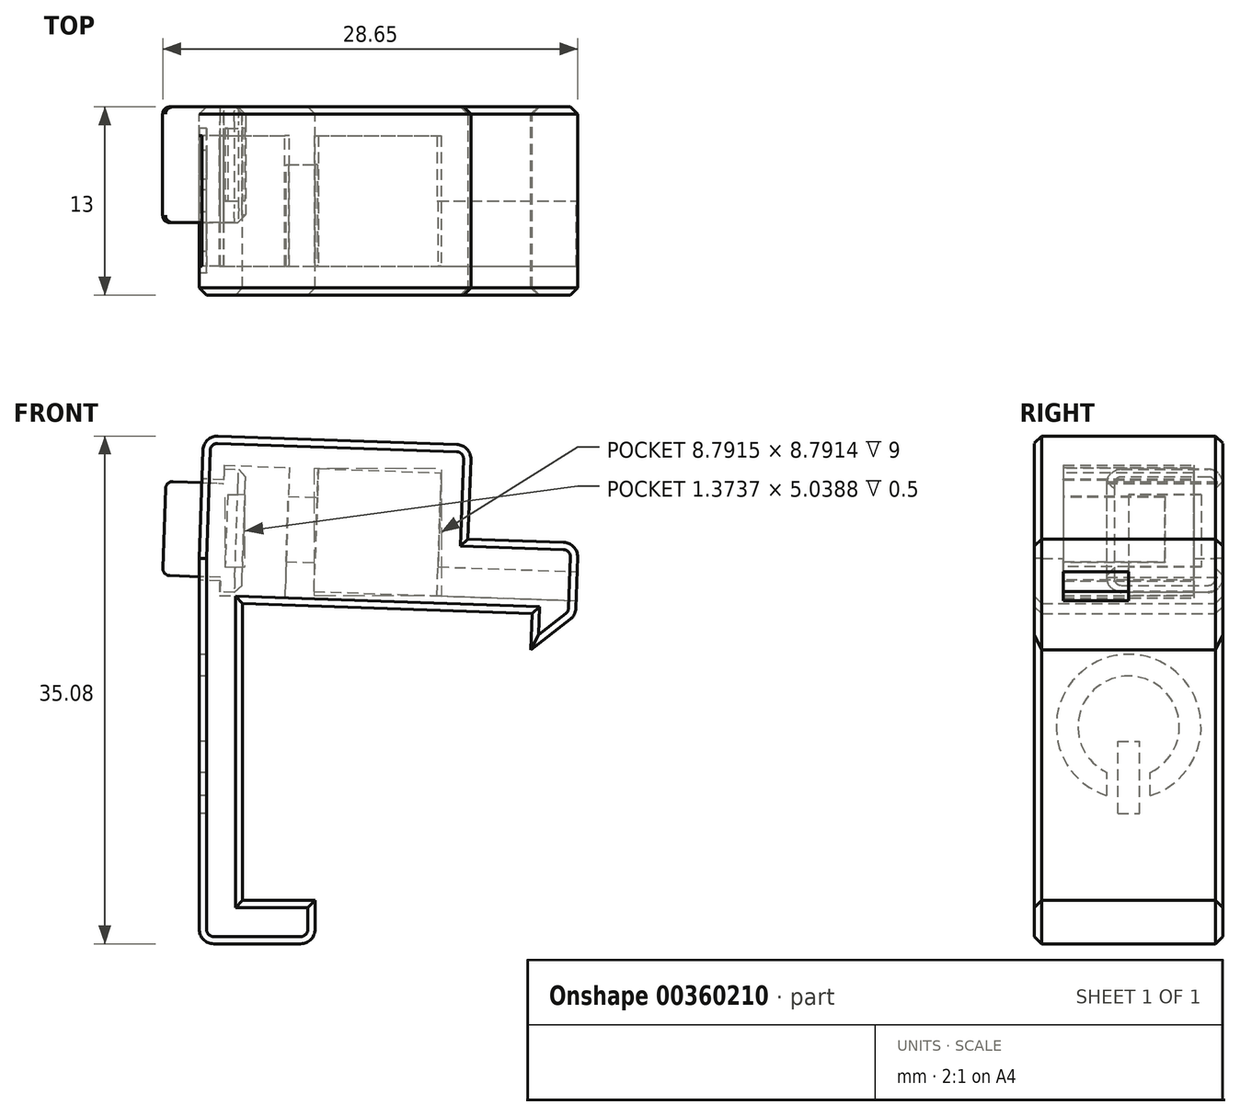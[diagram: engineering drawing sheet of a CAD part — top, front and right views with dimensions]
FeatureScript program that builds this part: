
annotation { "Feature Type Name" : "Feature", "Feature Type Description" : "" }
export const myFeature = defineFeature(function(context is Context, id is Id, definition is map)
    precondition{}
    {
        {
            var Q0;
            Q0=qCreatedBy(makeId("Front.planeOp"),FACE);
            var sketch = newSketch(context, id + "F0", { "sketchPlane" : qUnion([Q0])});
            skLineSegment(sketch, "E0", {"start": v(5, 0) * mm, "end": v(0, 0) * mm});
            skLineSegment(sketch, "E1", {"start": v(0, 0) * mm, "end": v(0, 20.51) * mm});
            skLineSegment(sketch, "E2", {"start": v(0, 20.51) * mm, "end": v(19.99, 19.81) * mm});
            skLineSegment(sketch, "E3", {"start": v(19.99, 19.81) * mm, "end": v(19.9, 17.32) * mm});
            skLineSegment(sketch, "E4", {"start": v(19.9, 17.32) * mm, "end": v(22.99, 19.7) * mm});
            skLineSegment(sketch, "E5", {"start": v(22.99, 19.7) * mm, "end": v(23.1, 22.7) * mm});
            skLineSegment(sketch, "E6", {"start": v(23.1, 22.7) * mm, "end": v(-3, 23.62) * mm});
            skLineSegment(sketch, "E7", {"start": v(-3, 23.62) * mm, "end": v(-3, -3) * mm});
            skLineSegment(sketch, "E8", {"start": v(-3, -3) * mm, "end": v(5, -3) * mm});
            skLineSegment(sketch, "E9", {"start": v(5, -3) * mm, "end": v(5, 0) * mm});
            skPoint(sketch, "E10.orphan", {"position": v(0, 20.51) * mm});
            skSolve(sketch);
        }
        {
            var Q0;
            Q0=qSketchRegion(id+"F0",true);
            extrude(context, id + "F1", {"entities" : qUnion([Q0]), "depth" : 13 * mm});
        }
        {
            var Q0;
            Q0=makeQuery(id+"F1.opExtrude","SWEPT_EDGE",EDGE,{"disambiguationData":[OSD([sQuery(id+"F0.wireOp",EDGE,"E8"),sQuery(id+"F0.wireOp",EDGE,"E9")])]});
            var Q1;
            Q1=makeQuery(id+"F1.opExtrude","SWEPT_EDGE",EDGE,{"disambiguationData":[OSD([sQuery(id+"F0.wireOp",EDGE,"E8"),sQuery(id+"F0.wireOp",EDGE,"E9")])]});
            var Q2;
            Q2=makeQuery(id+"F1.opExtrude","SWEPT_EDGE",EDGE,{"disambiguationData":[OSD([sQuery(id+"F0.wireOp",EDGE,"E4"),sQuery(id+"F0.wireOp",EDGE,"E5")])]});
            fillet(context, id + "F2", {"entities" : qUnion([Q0, Q1, Q2]), "radius" : 1 * mm, "tangentPropagation" : true, "allowEdgeOverflow" : false});
        }
        {
            var Q0;
            Q0=makeQuery(id+"F1.opExtrude","SWEPT_FACE",FACE,{"disambiguationData":[OSD([sQuery(id+"F0.wireOp",EDGE,"E6")])]});
            var sketch = newSketch(context, id + "F3", { "sketchPlane" : qUnion([Q0])});
            skLineSegment(sketch, "E11.bottom", {"start": v(4.18, -2) * mm, "end": v(12.68, -2) * mm});
            skLineSegment(sketch, "E11.top", {"start": v(4.18, -11) * mm, "end": v(12.68, -11) * mm});
            skLineSegment(sketch, "E11.left", {"start": v(4.18, -2) * mm, "end": v(4.18, -11) * mm});
            skLineSegment(sketch, "E11.right", {"start": v(12.68, -2) * mm, "end": v(12.68, -11) * mm});
            skLineSegment(sketch, "E12.bottom", {"start": v(12.68, -11) * mm, "end": v(22.28, -11) * mm});
            skLineSegment(sketch, "E12.top", {"start": v(12.68, -6.5) * mm, "end": v(22.28, -6.5) * mm});
            skLineSegment(sketch, "E12.left", {"start": v(12.68, -11) * mm, "end": v(12.68, -6.5) * mm});
            skLineSegment(sketch, "E12.right", {"start": v(22.28, -11) * mm, "end": v(22.28, -6.5) * mm});
            skSolve(sketch);
        }
        {
            var Q0;
            Q0 = qSketchRegion(id + "F3", true);
            extrude(context, id + "F4", {"entities" : qUnion([Q0]), "operationType" : NewBodyOperationType.REMOVE, "oppositeDirection" : true, "depth" : 2 * mm});
        }
        {
            var Q0;
            Q0=makeQuery(id+"F1.opExtrude","SWEPT_FACE",FACE,{"disambiguationData":[OSD([sQuery(id+"F0.wireOp",EDGE,"E6")])]});
            var sketch = newSketch(context, id + "F5", { "sketchPlane" : qUnion([Q0])});
            skLineSegment(sketch, "E13.top", {"start": v(14.68, -13) * mm, "end": v(22.28, -13) * mm});
            skLineSegment(sketch, "E13.left", {"start": v(14.68, -4.5) * mm, "end": v(14.68, -13) * mm});
            skLineSegment(sketch, "E13.right", {"start": v(22.28, -4.48) * mm, "end": v(22.28, -13) * mm});
            skLineSegment(sketch, "E14", {"start": v(14.68, -4.5) * mm, "end": v(14.68, 0) * mm});
            skLineSegment(sketch, "E15", {"start": v(14.68, 0) * mm, "end": v(22.28, 0) * mm});
            skLineSegment(sketch, "E16", {"start": v(22.28, 0) * mm, "end": v(22.28, -4.48) * mm});
            skSolve(sketch);
        }
        {
            var Q0;
            Q0 = qSketchRegion(id + "F5", true);
            extrude(context, id + "F6", {"entities" : qUnion([Q0]), "operationType" : NewBodyOperationType.ADD, "depth" : 2 * mm});
        }
        {
            var Q0;
            Q0=makeQuery(id+"F1.opExtrude","SWEPT_FACE",FACE,{"disambiguationData":[OSD([sQuery(id+"F0.wireOp",EDGE,"E6")])]});
            var sketch = newSketch(context, id + "F7", { "sketchPlane" : qUnion([Q0])});
            skSolve(sketch);
        }
        {
            var Q0;
            {var subQ3=sQuery(id+"F0.wireOp",EDGE,"E6");Q0=makeQuery(id+"F7.imprint","IMPRINT",FACE,{"disambiguationData":[TD([[makeQuery(id+"F7.imprint","IMPRINT",EDGE,{"derivedFrom":makeQuery(id+"F1.opExtrude","CAP_EDGE",EDGE,{"disambiguationData":[OSD([subQ3])],"isStart":true})}),1.0]])]});}
            var sketch = newSketch(context, id + "F8", { "sketchPlane" : qUnion([Q0])});
            skLineSegment(sketch, "E17", {"start": v(14.68, -13) * mm, "end": v(-3.82, -13) * mm});
            skLineSegment(sketch, "E18", {"start": v(-3.82, -13) * mm, "end": v(-3.82, -11) * mm});
            skLineSegment(sketch, "E19", {"start": v(-3.82, -11) * mm, "end": v(4.18, -11) * mm});
            skLineSegment(sketch, "E20", {"start": v(4.18, -11) * mm, "end": v(4.18, -11) * mm});
            skLineSegment(sketch, "E21", {"start": v(4.18, -11) * mm, "end": v(12.68, -11) * mm});
            skLineSegment(sketch, "E22", {"start": v(14.68, 0) * mm, "end": v(-3.82, 0) * mm});
            skLineSegment(sketch, "E23", {"start": v(-3.82, 0) * mm, "end": v(-3.82, -4) * mm});
            skLineSegment(sketch, "E24", {"start": v(-3.82, -4) * mm, "end": v(4.18, -4) * mm});
            skLineSegment(sketch, "E25", {"start": v(4.18, -4) * mm, "end": v(4.18, -2) * mm});
            skLineSegment(sketch, "E26", {"start": v(4.18, -2) * mm, "end": v(12.68, -2) * mm});
            skLineSegment(sketch, "E27", {"start": v(12.68, -2) * mm, "end": v(12.68, -11) * mm});
            skLineSegment(sketch, "E28", {"start": v(14.68, -13) * mm, "end": v(14.68, 0) * mm});
            skSolve(sketch);
        }
        {
            var Q0;
            Q0 = qSketchRegion(id + "F8", true);
            extrude(context, id + "F9", {"entities" : qUnion([Q0]), "operationType" : NewBodyOperationType.ADD, "depth" : 4.5 * mm});
        }
        {
            var Q0;
            Q0=makeQuery(id+"F9.opExtrude","CAP_FACE",FACE,{"disambiguationData":[OSD([sQuery(id+"F8.wireOp",EDGE,"E17"),sQuery(id+"F8.wireOp",EDGE,"E18"),sQuery(id+"F8.wireOp",EDGE,"E19"),sQuery(id+"F8.wireOp",EDGE,"E20"),sQuery(id+"F8.wireOp",EDGE,"E21"),sQuery(id+"F8.wireOp",EDGE,"E22"),sQuery(id+"F8.wireOp",EDGE,"E23"),sQuery(id+"F8.wireOp",EDGE,"E24"),sQuery(id+"F8.wireOp",EDGE,"E25"),sQuery(id+"F8.wireOp",EDGE,"E26"),sQuery(id+"F8.wireOp",EDGE,"E27"),sQuery(id+"F8.wireOp",EDGE,"E28")])],"isStart":false});
            var sketch = newSketch(context, id + "F10", { "sketchPlane" : qUnion([Q0])});
            skLineSegment(sketch, "E29.bottom", {"start": v(-3.82, 0) * mm, "end": v(14.68, 0) * mm});
            skLineSegment(sketch, "E29.top", {"start": v(-3.82, -13) * mm, "end": v(14.68, -13) * mm});
            skLineSegment(sketch, "E29.left", {"start": v(-3.82, 0) * mm, "end": v(-3.82, -13) * mm});
            skLineSegment(sketch, "E29.right", {"start": v(14.68, 0) * mm, "end": v(14.68, -13) * mm});
            skLineSegment(sketch, "E30.bottom", {"start": v(4.18, -2) * mm, "end": v(12.68, -2) * mm});
            skLineSegment(sketch, "E30.top", {"start": v(4.18, -11) * mm, "end": v(12.68, -11) * mm});
            skLineSegment(sketch, "E30.left", {"start": v(4.18, -2) * mm, "end": v(4.18, -11) * mm});
            skLineSegment(sketch, "E30.right", {"start": v(12.68, -2) * mm, "end": v(12.68, -11) * mm});
            skSolve(sketch);
        }
        {
            var Q0;
            Q0 = qSketchRegion(id + "F10", true);
            extrude(context, id + "F11", {"entities" : qUnion([Q0]), "operationType" : NewBodyOperationType.ADD, "depth" : 2 * mm});
        }
        {
            var Q0;
            Q0=makeQuery(id+"F11.opExtrude","CAP_FACE",FACE,{"disambiguationData":[OSD([sQuery(id+"F10.wireOp",EDGE,"E29.bottom"),sQuery(id+"F10.wireOp",EDGE,"E29.top"),sQuery(id+"F10.wireOp",EDGE,"E29.left"),sQuery(id+"F10.wireOp",EDGE,"E29.right"),sQuery(id+"F10.wireOp",EDGE,"E30.bottom"),sQuery(id+"F10.wireOp",EDGE,"E30.top"),sQuery(id+"F10.wireOp",EDGE,"E30.left"),sQuery(id+"F10.wireOp",EDGE,"E30.right")])],"isStart":false});
            var sketch = newSketch(context, id + "F12", { "sketchPlane" : qUnion([Q0])});
            skLineSegment(sketch, "E31.bottom", {"start": v(14.68, -13) * mm, "end": v(-3.82, -13) * mm});
            skLineSegment(sketch, "E31.top", {"start": v(14.68, 0) * mm, "end": v(-3.82, 0) * mm});
            skLineSegment(sketch, "E31.left", {"start": v(14.68, -13) * mm, "end": v(14.68, 0) * mm});
            skLineSegment(sketch, "E31.right", {"start": v(-3.82, -13) * mm, "end": v(-3.82, 0) * mm});
            skSolve(sketch);
        }
        {
            var Q0;
            Q0 = qSketchRegion(id + "F12", true);
            extrude(context, id + "F13", {"entities" : qUnion([Q0]), "operationType" : NewBodyOperationType.ADD, "depth" : 2 * mm});
        }
        {
            var Q0;
            Q0=makeQuery(id+"F13.boolean.opBoolean","MERGE",FACE,{"derivedFrom":[makeQuery(id+"F11.boolean.opBoolean","MERGE",FACE,{"derivedFrom":[makeQuery(id+"F9.opExtrude","SWEPT_FACE",FACE,{"disambiguationData":[OSD([sQuery(id+"F8.wireOp",EDGE,"E18")])]}),makeQuery(id+"F9.opExtrude","SWEPT_FACE",FACE,{"disambiguationData":[OSD([sQuery(id+"F8.wireOp",EDGE,"E23")])]}),makeQuery(id+"F11.opExtrude","SWEPT_FACE",FACE,{"disambiguationData":[OSD([sQuery(id+"F10.wireOp",EDGE,"E29.left")])]})]}),makeQuery(id+"F13.opExtrude","SWEPT_FACE",FACE,{"disambiguationData":[OSD([sQuery(id+"F12.wireOp",EDGE,"E31.right")])]})]});
            var sketch = newSketch(context, id + "F14", { "sketchPlane" : qUnion([Q0])});
            skLineSegment(sketch, "E32.bottom", {"start": v(11, 29) * mm, "end": v(2, 29) * mm});
            skLineSegment(sketch, "E32.top", {"start": v(11, 22) * mm, "end": v(2, 22) * mm});
            skLineSegment(sketch, "E32.left", {"start": v(11, 29) * mm, "end": v(11, 22) * mm});
            skLineSegment(sketch, "E32.right", {"start": v(2, 29) * mm, "end": v(2, 22) * mm});
            skSolve(sketch);
        }
        {
            var Q0;
            Q0 = qSketchRegion(id + "F14", true);
            extrude(context, id + "F15", {"entities" : qUnion([Q0]), "operationType" : NewBodyOperationType.REMOVE, "oppositeDirection" : true, "depth" : 6 * mm});
        }
        {
            var Q0;
            Q0=makeQuery(id+"F15.boolean.opBoolean","COPY",FACE,{"derivedFrom":makeQuery(id+"F15.opExtrude","SWEPT_FACE",FACE,{"disambiguationData":[OSD([sQuery(id+"F14.wireOp",EDGE,"E32.right")])]})});
            var sketch = newSketch(context, id + "F16", { "sketchPlane" : qUnion([Q0])});
            skLineSegment(sketch, "E33.bottom", {"start": v(-1.27, 30.06) * mm, "end": v(3.22, 29.9) * mm});
            skLineSegment(sketch, "E33.top", {"start": v(-1.59, 21.07) * mm, "end": v(2.9, 20.91) * mm});
            skLineSegment(sketch, "E33.left", {"start": v(-1.27, 30.06) * mm, "end": v(-1.59, 21.07) * mm});
            skLineSegment(sketch, "E33.right", {"start": v(3.22, 29.9) * mm, "end": v(2.9, 20.91) * mm});
            skSolve(sketch);
        }
        {
            var Q0;
            Q0 = qSketchRegion(id + "F16", true);
            var Q1;
            Q1=makeQuery(id+"F15.boolean.opBoolean","MERGE",FACE,{"derivedFrom":[makeQuery(id+"F11.boolean.opBoolean","MERGE",FACE,{"derivedFrom":[makeQuery(id+"F9.boolean.opBoolean","MERGE",FACE,{"derivedFrom":[makeQuery(id+"F4.boolean.opBoolean","COPY",FACE,{"derivedFrom":makeQuery(id+"F4.opExtrude","SWEPT_FACE",FACE,{"disambiguationData":[OSD([sQuery(id+"F3.wireOp",EDGE,"E11.top"),sQuery(id+"F3.wireOp",EDGE,"E12.bottom")])]})}),makeQuery(id+"F9.opExtrude","SWEPT_FACE",FACE,{"disambiguationData":[OSD([sQuery(id+"F8.wireOp",EDGE,"E19"),sQuery(id+"F8.wireOp",EDGE,"E21")])]})]}),makeQuery(id+"F11.opExtrude","SWEPT_FACE",FACE,{"disambiguationData":[OSD([sQuery(id+"F10.wireOp",EDGE,"E30.top")])]})]}),makeQuery(id+"F15.opExtrude","SWEPT_FACE",FACE,{"disambiguationData":[OSD([sQuery(id+"F14.wireOp",EDGE,"E32.left")])]})]});
            extrude(context, id + "F17", {"entities" : qUnion([Q0]), "operationType" : NewBodyOperationType.REMOVE, "endBound" : BoundingType.UP_TO_SURFACE, "depth" : 25 * mm, "endBoundEntityFace" : qUnion([Q1]), "offsetDistance" : 25 * mm});
        }
        {
            var Q0;
            Q0=qCreatedBy(makeId("Front.planeOp"),FACE);
            var sketch = newSketch(context, id + "F18", { "sketchPlane" : qUnion([Q0])});
            skLineSegment(sketch, "E34", {"start": v(0.22, 29.76) * mm, "end": v(-0.08, 21.27) * mm});
            skLineSegment(sketch, "E35", {"start": v(-0.08, 21.27) * mm, "end": v(-1.58, 21.32) * mm});
            skLineSegment(sketch, "E36", {"start": v(-1.58, 21.32) * mm, "end": v(-1.54, 22.32) * mm});
            skLineSegment(sketch, "E37", {"start": v(-1.54, 22.32) * mm, "end": v(-5.54, 22.46) * mm});
            skLineSegment(sketch, "E38", {"start": v(-5.54, 22.46) * mm, "end": v(-5.32, 28.95) * mm});
            skLineSegment(sketch, "E39", {"start": v(-5.32, 28.95) * mm, "end": v(-1.32, 28.81) * mm});
            skLineSegment(sketch, "E40", {"start": v(-1.32, 28.81) * mm, "end": v(-1.28, 29.81) * mm});
            skLineSegment(sketch, "E41", {"start": v(-1.28, 29.81) * mm, "end": v(0.22, 29.76) * mm});
            skSolve(sketch);
        }
        {
            var Q0;
            Q0 = qSketchRegion(id + "F18", true);
            extrude(context, id + "F19", {"entities" : qUnion([Q0]), "depth" : 8 * mm, "offsetDistance" : 25 * mm});
        }
        {
            var Q0;
            Q0=makeQuery(id+"F19.opExtrude","SWEPT_FACE",FACE,{"disambiguationData":[OSD([sQuery(id+"F18.wireOp",EDGE,"E38")])]});
            fillet(context, id + "F20", {"entities" : qUnion([Q0]), "radius" : 0.5 * mm, "tangentPropagation" : true, "allowEdgeOverflow" : false});
        }
        {
            var Q0;
            Q0=makeQuery(id+"F19.opExtrude","CAP_EDGE",EDGE,{"disambiguationData":[OSD([sQuery(id+"F18.wireOp",EDGE,"E41")])],"isStart":false});
            var Q1;
            Q1=makeQuery(id+"F19.opExtrude","CAP_EDGE",EDGE,{"disambiguationData":[OSD([sQuery(id+"F18.wireOp",EDGE,"E41")])],"isStart":true});
            var Q2;
            Q2=makeQuery(id+"F19.opExtrude","CAP_EDGE",EDGE,{"disambiguationData":[OSD([sQuery(id+"F18.wireOp",EDGE,"E35")])],"isStart":true});
            var Q3;
            Q3=makeQuery(id+"F19.opExtrude","CAP_EDGE",EDGE,{"disambiguationData":[OSD([sQuery(id+"F18.wireOp",EDGE,"E35")])],"isStart":false});
            fillet(context, id + "F21", {"entities" : qUnion([Q0, Q1, Q2, Q3]), "radius" : 1 * mm, "tangentPropagation" : true, "allowEdgeOverflow" : false});
        }
        {
            var Q0;
            Q0=makeQuery(id+"F19.opExtrude","CAP_EDGE",EDGE,{"disambiguationData":[OSD([sQuery(id+"F18.wireOp",EDGE,"E34")])],"isStart":false});
            chamfer(context, id + "F22", {"entities" : qUnion([Q0]), "width" : 0.5 * mm, "tangentPropagation" : true});
        }
        {
            var Q0;
            Q0=makeQuery(id+"F1.opExtrude","SWEPT_FACE",FACE,{"disambiguationData":[OSD([sQuery(id+"F0.wireOp",EDGE,"E7")])]});
            var sketch = newSketch(context, id + "F23", { "sketchPlane" : qUnion([Q0])});
            skLineSegment(sketch, "E42.bottom", {"start": v(7.25, 6) * mm, "end": v(5.75, 6) * mm});
            skLineSegment(sketch, "E42.top", {"start": v(7.25, 11) * mm, "end": v(5.75, 11) * mm});
            skLineSegment(sketch, "E42.left", {"start": v(7.25, 6) * mm, "end": v(7.25, 11) * mm});
            skLineSegment(sketch, "E42.right", {"start": v(5.75, 6) * mm, "end": v(5.75, 11) * mm});
            skLineSegment(sketch, "E43.left", {"start": v(8, 7.23) * mm, "end": v(8, 8.84) * mm});
            skLineSegment(sketch, "E43.right", {"start": v(5, 7.23) * mm, "end": v(5, 8.84) * mm});
            skPoint(sketch, "E44", {"position": v(6.5, 6) * mm});
            skArc(sketch, "E45.trimOffspring", {"start": v(8, 7.23) * mm, "mid": v(6.5, 17) * mm, "end": v(5, 7.23) * mm});
            skArc(sketch, "E46.trimOffspring", {"start": v(8, 8.84) * mm, "mid": v(6.5, 15.5) * mm, "end": v(5, 8.84) * mm});
            skSolve(sketch);
        }
        {
            var Q0;
            Q0 = qSketchRegion(id + "F23", true);
            extrude(context, id + "F24", {"entities" : qUnion([Q0]), "operationType" : NewBodyOperationType.REMOVE, "oppositeDirection" : true, "depth" : 0.5 * mm, "offsetDistance" : 25 * mm});
        }
        {
            var Q0;
            Q0=makeQuery(id+"F1.opExtrude","SWEPT_EDGE",EDGE,{"disambiguationData":[OSD([sQuery(id+"F0.wireOp",EDGE,"E7"),sQuery(id+"F0.wireOp",EDGE,"E8")])]});
            var Q1;
            Q1=makeQuery(id+"F13.opExtrude","CAP_EDGE",EDGE,{"disambiguationData":[OSD([sQuery(id+"F12.wireOp",EDGE,"E31.right")])],"isStart":false});
            var Q2;
            Q2=makeQuery(id+"F13.opExtrude","CAP_EDGE",EDGE,{"disambiguationData":[OSD([sQuery(id+"F12.wireOp",EDGE,"E31.left")])],"isStart":false});
            var Q3;
            Q3=makeQuery(id+"F6.opExtrude","CAP_EDGE",EDGE,{"disambiguationData":[OSD([sQuery(id+"F5.wireOp",EDGE,"E13.right"),sQuery(id+"F5.wireOp",EDGE,"E16")])],"isStart":false});
            fillet(context, id + "F25", {"entities" : qUnion([Q0, Q1, Q2, Q3]), "radius" : 1 * mm, "tangentPropagation" : true, "allowEdgeOverflow" : false});
        }
        {
            var Q0;
            Q0=makeQuery(id+"F13.boolean.opBoolean","MERGE",FACE,{"derivedFrom":[makeQuery(id+"F11.boolean.opBoolean","MERGE",FACE,{"derivedFrom":[makeQuery(id+"F9.boolean.opBoolean","MERGE",FACE,{"derivedFrom":[makeQuery(id+"F6.boolean.opBoolean","MERGE",FACE,{"derivedFrom":[makeQuery(id+"F1.opExtrude","CAP_FACE",FACE,{"disambiguationData":[OSD([sQuery(id+"F0.wireOp",EDGE,"E0"),sQuery(id+"F0.wireOp",EDGE,"E1"),sQuery(id+"F0.wireOp",EDGE,"E2"),sQuery(id+"F0.wireOp",EDGE,"E3"),sQuery(id+"F0.wireOp",EDGE,"E4"),sQuery(id+"F0.wireOp",EDGE,"E5"),sQuery(id+"F0.wireOp",EDGE,"E6"),sQuery(id+"F0.wireOp",EDGE,"E7"),sQuery(id+"F0.wireOp",EDGE,"E8"),sQuery(id+"F0.wireOp",EDGE,"E9")])],"isStart":false}),makeQuery(id+"F6.opExtrude","SWEPT_FACE",FACE,{"disambiguationData":[OSD([sQuery(id+"F5.wireOp",EDGE,"E13.top")])]})]}),makeQuery(id+"F9.opExtrude","SWEPT_FACE",FACE,{"disambiguationData":[OSD([sQuery(id+"F8.wireOp",EDGE,"E17")])]})]}),makeQuery(id+"F11.opExtrude","SWEPT_FACE",FACE,{"disambiguationData":[OSD([sQuery(id+"F10.wireOp",EDGE,"E29.top")])]})]}),makeQuery(id+"F13.opExtrude","SWEPT_FACE",FACE,{"disambiguationData":[OSD([sQuery(id+"F12.wireOp",EDGE,"E31.bottom")])]})]});
            var Q1;
            Q1=makeQuery(id+"F13.boolean.opBoolean","MERGE",FACE,{"derivedFrom":[makeQuery(id+"F11.boolean.opBoolean","MERGE",FACE,{"derivedFrom":[makeQuery(id+"F9.boolean.opBoolean","MERGE",FACE,{"derivedFrom":[makeQuery(id+"F6.boolean.opBoolean","MERGE",FACE,{"derivedFrom":[makeQuery(id+"F1.opExtrude","CAP_FACE",FACE,{"disambiguationData":[OSD([sQuery(id+"F0.wireOp",EDGE,"E0"),sQuery(id+"F0.wireOp",EDGE,"E1"),sQuery(id+"F0.wireOp",EDGE,"E2"),sQuery(id+"F0.wireOp",EDGE,"E3"),sQuery(id+"F0.wireOp",EDGE,"E4"),sQuery(id+"F0.wireOp",EDGE,"E5"),sQuery(id+"F0.wireOp",EDGE,"E6"),sQuery(id+"F0.wireOp",EDGE,"E7"),sQuery(id+"F0.wireOp",EDGE,"E8"),sQuery(id+"F0.wireOp",EDGE,"E9")])],"isStart":true}),makeQuery(id+"F6.opExtrude","SWEPT_FACE",FACE,{"disambiguationData":[OSD([sQuery(id+"F5.wireOp",EDGE,"E15")])]})]}),makeQuery(id+"F9.opExtrude","SWEPT_FACE",FACE,{"disambiguationData":[OSD([sQuery(id+"F8.wireOp",EDGE,"E22")])]})]}),makeQuery(id+"F11.opExtrude","SWEPT_FACE",FACE,{"disambiguationData":[OSD([sQuery(id+"F10.wireOp",EDGE,"E29.bottom")])]})]}),makeQuery(id+"F13.opExtrude","SWEPT_FACE",FACE,{"disambiguationData":[OSD([sQuery(id+"F12.wireOp",EDGE,"E31.top")])]})]});
            chamfer(context, id + "F26", {"entities" : qUnion([Q0, Q1]), "width" : 0.5 * mm, "tangentPropagation" : true});
        }
        {
            var Q0;
            Q0=makeQuery(id+"F19.opExtrude","SWEPT_FACE",FACE,{"disambiguationData":[OSD([sQuery(id+"F18.wireOp",EDGE,"E34")])]});
            var sketch = newSketch(context, id + "F27", { "sketchPlane" : qUnion([Q0])});
            skLineSegment(sketch, "E47.bottom", {"start": v(-1.5, 28) * mm, "end": v(-6.5, 28) * mm});
            skLineSegment(sketch, "E47.top", {"start": v(-1.5, 23) * mm, "end": v(-6.5, 23) * mm});
            skLineSegment(sketch, "E47.left", {"start": v(-1.5, 28) * mm, "end": v(-1.5, 23) * mm});
            skLineSegment(sketch, "E47.right", {"start": v(-6.5, 28) * mm, "end": v(-6.5, 23) * mm});
            skPoint(sketch, "E48", {"position": v(-4, 28) * mm});
            skPoint(sketch, "E49", {"position": v(-1.5, 25.5) * mm});
            skSolve(sketch);
        }
        {
            var Q0;
            Q0 = qSketchRegion(id + "F27", true);
            extrude(context, id + "F28", {"entities" : qUnion([Q0]), "operationType" : NewBodyOperationType.REMOVE, "oppositeDirection" : true, "depth" : 1.2 * mm, "offsetDistance" : 25 * mm});
        }
    });
